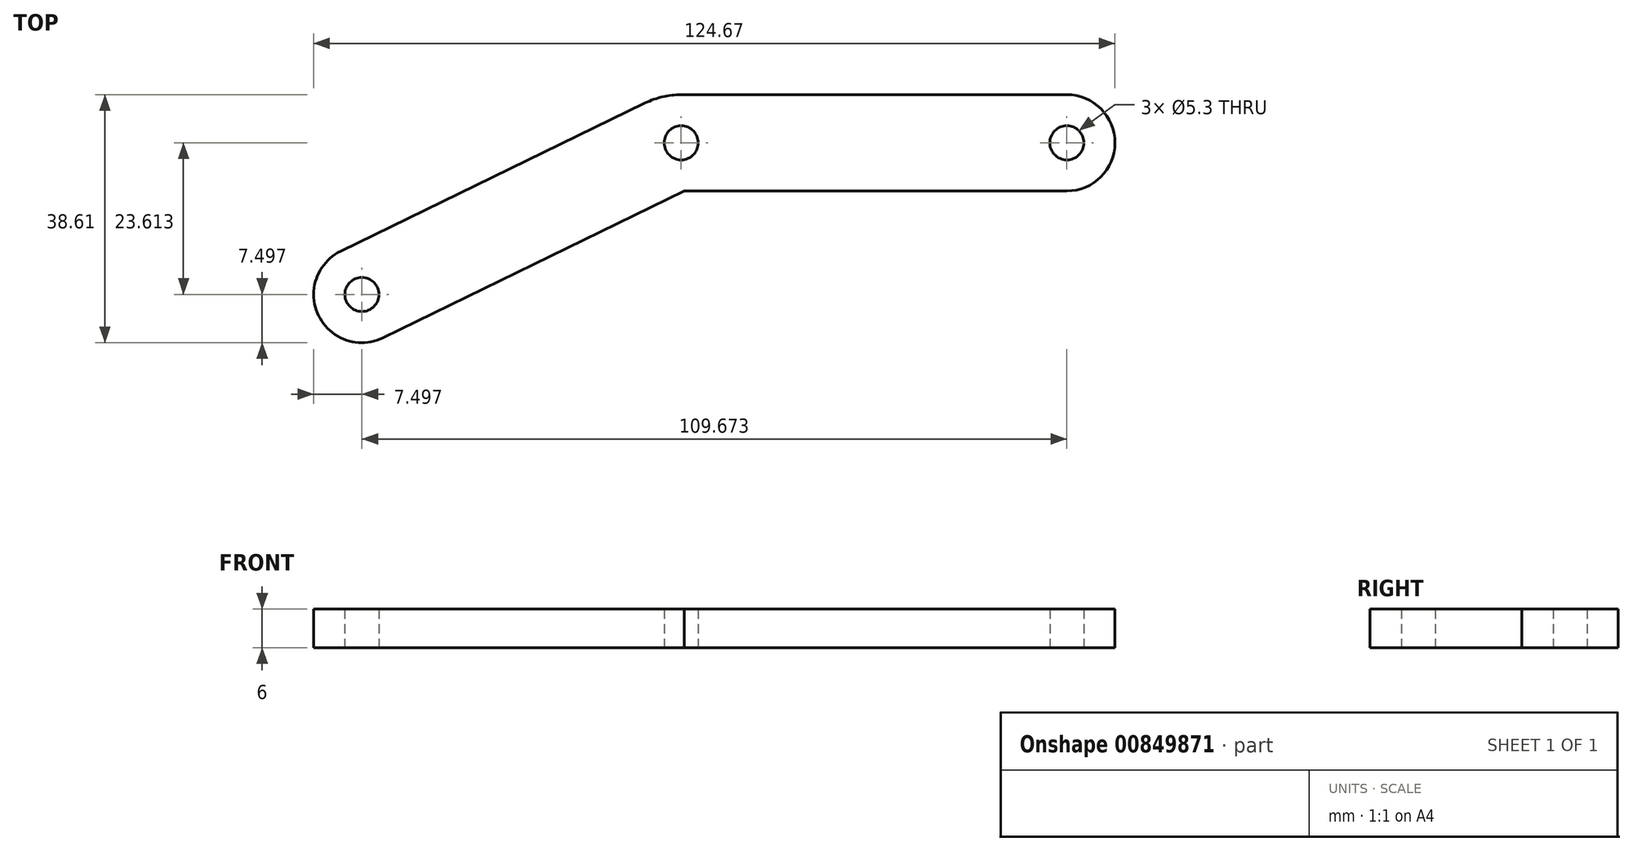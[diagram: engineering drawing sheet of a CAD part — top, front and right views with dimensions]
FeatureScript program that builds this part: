
annotation { "Feature Type Name" : "Feature", "Feature Type Description" : "" }
export const myFeature = defineFeature(function(context is Context, id is Id, definition is map)
    precondition{}
    {
        {
            var Q0;
            Q0=qCreatedBy(makeId("Top.planeOp"),FACE);
            var sketch = newSketch(context, id + "F0", { "sketchPlane" : qUnion([Q0])});
            skArc(sketch, "E0", {"start": v(60, -7.5) * mm, "mid": v(67.5, 0) * mm, "end": v(60, 7.5) * mm});
            skArc(sketch, "E1", {"start": v(-52.96, -16.87) * mm, "mid": v(-56.42, -26.9) * mm, "end": v(-46.39, -30.36) * mm});
            skLineSegment(sketch, "E2", {"start": v(-52.96, -16.87) * mm, "end": v(-5.6, 6.2) * mm});
            skLineSegment(sketch, "E3", {"start": v(0, 7.5) * mm, "end": v(60, 7.5) * mm});
            skLineSegment(sketch, "E4", {"start": v(60, -7.5) * mm, "end": v(0.5, -7.5) * mm});
            skLineSegment(sketch, "E5", {"start": v(-46.39, -30.36) * mm, "end": v(0.5, -7.5) * mm});
            skCircle(sketch, "E6", {"center": v(0, 0) * mm, "radius": 2.65 * mm});
            skCircle(sketch, "E7", {"center": v(60, 0) * mm, "radius": 2.65 * mm});
            skCircle(sketch, "E8", {"center": v(-49.67, -23.61) * mm, "radius": 2.65 * mm});
            skArc(sketch, "E9.trimOffspring", {"start": v(0, 7.5) * mm, "mid": v(-2.88, 7.17) * mm, "end": v(-5.6, 6.2) * mm});
            skPoint(sketch, "E10.orphan", {"position": v(0, -7.5) * mm});
            skSolve(sketch);
        }
        {
            var Q0;
            Q0=makeQuery(id+"F0.imprint","IMPRINT",FACE,{"disambiguationData":[TD([[makeQuery(id+"F0.imprint","IMPRINT",EDGE,{"derivedFrom":sQuery(id+"F0.wireOp",EDGE,"E0")}),1.0]])]});
            extrude(context, id + "F1", {"entities" : qUnion([Q0]), "depth" : 6 * mm, "offsetDistance" : 25 * mm});
        }
    });
